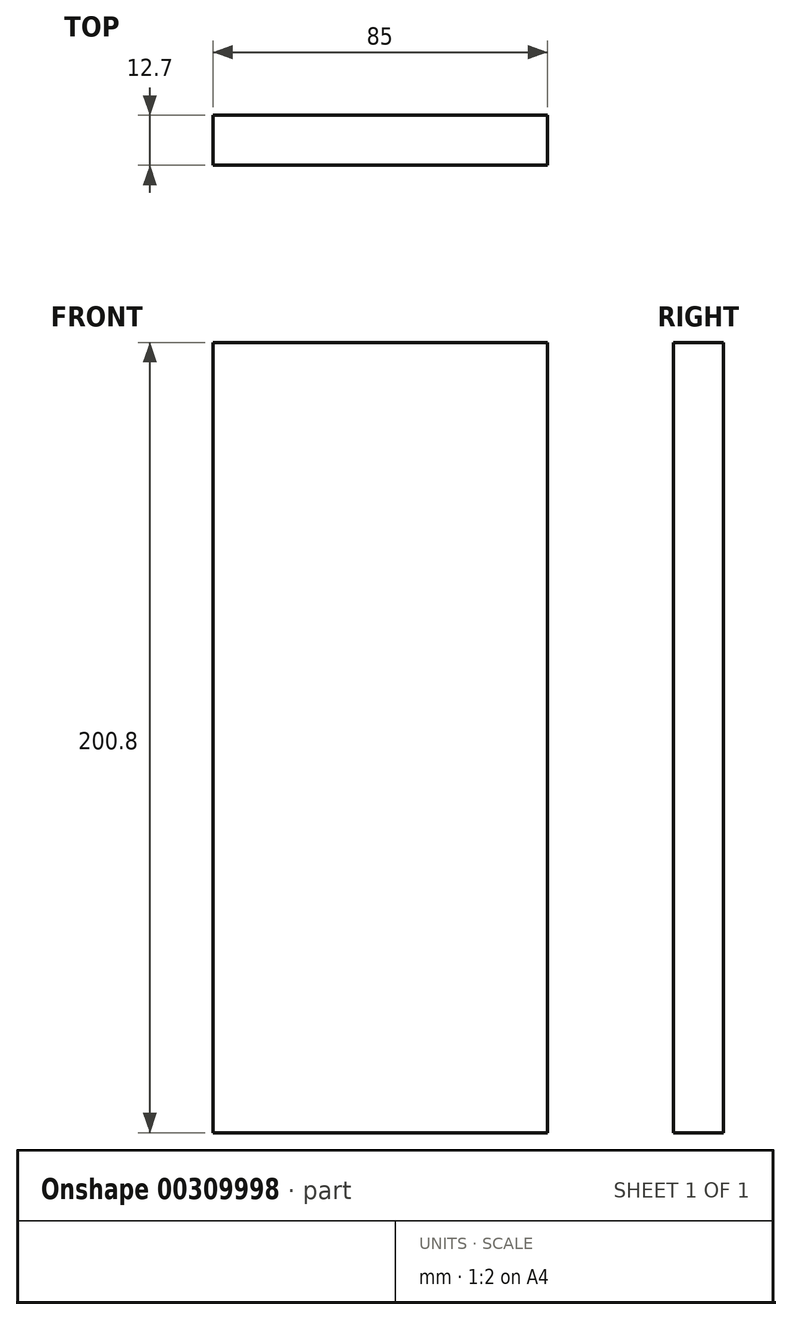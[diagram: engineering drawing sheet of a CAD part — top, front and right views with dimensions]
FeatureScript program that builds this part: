
annotation { "Feature Type Name" : "Feature", "Feature Type Description" : "" }
export const myFeature = defineFeature(function(context is Context, id is Id, definition is map)
    precondition{}
    {
        {
            var Q0;
            Q0=qCreatedBy(makeId("Front.planeOp"),FACE);
            var sketch = newSketch(context, id + "F0", { "sketchPlane" : qUnion([Q0])});
            skLineSegment(sketch, "E0.bottom", {"start": v(42.5, 100.4) * mm, "end": v(-42.5, 100.4) * mm});
            skLineSegment(sketch, "E0.top", {"start": v(42.5, -100.4) * mm, "end": v(-42.5, -100.4) * mm});
            skLineSegment(sketch, "E0.left", {"start": v(42.5, 100.4) * mm, "end": v(42.5, -100.4) * mm});
            skLineSegment(sketch, "E0.right", {"start": v(-42.5, 100.4) * mm, "end": v(-42.5, -100.4) * mm});
            skLineSegment(sketch, "E1", {"start": v(42.5, 100.4) * mm, "end": v(-42.5, -100.4) * mm, "construction": true});
            skSolve(sketch);
        }
        {
            var Q0;
            Q0=makeQuery(id+"F0.imprint","IMPRINT",FACE,{"disambiguationData":[TD([[makeQuery(id+"F0.imprint","IMPRINT",EDGE,{"derivedFrom":sQuery(id+"F0.wireOp",EDGE,"E0.bottom")}),1.0]])]});
            extrude(context, id + "F1", {"entities" : qUnion([Q0]), "depth" : 12.7 * mm});
        }
    });
